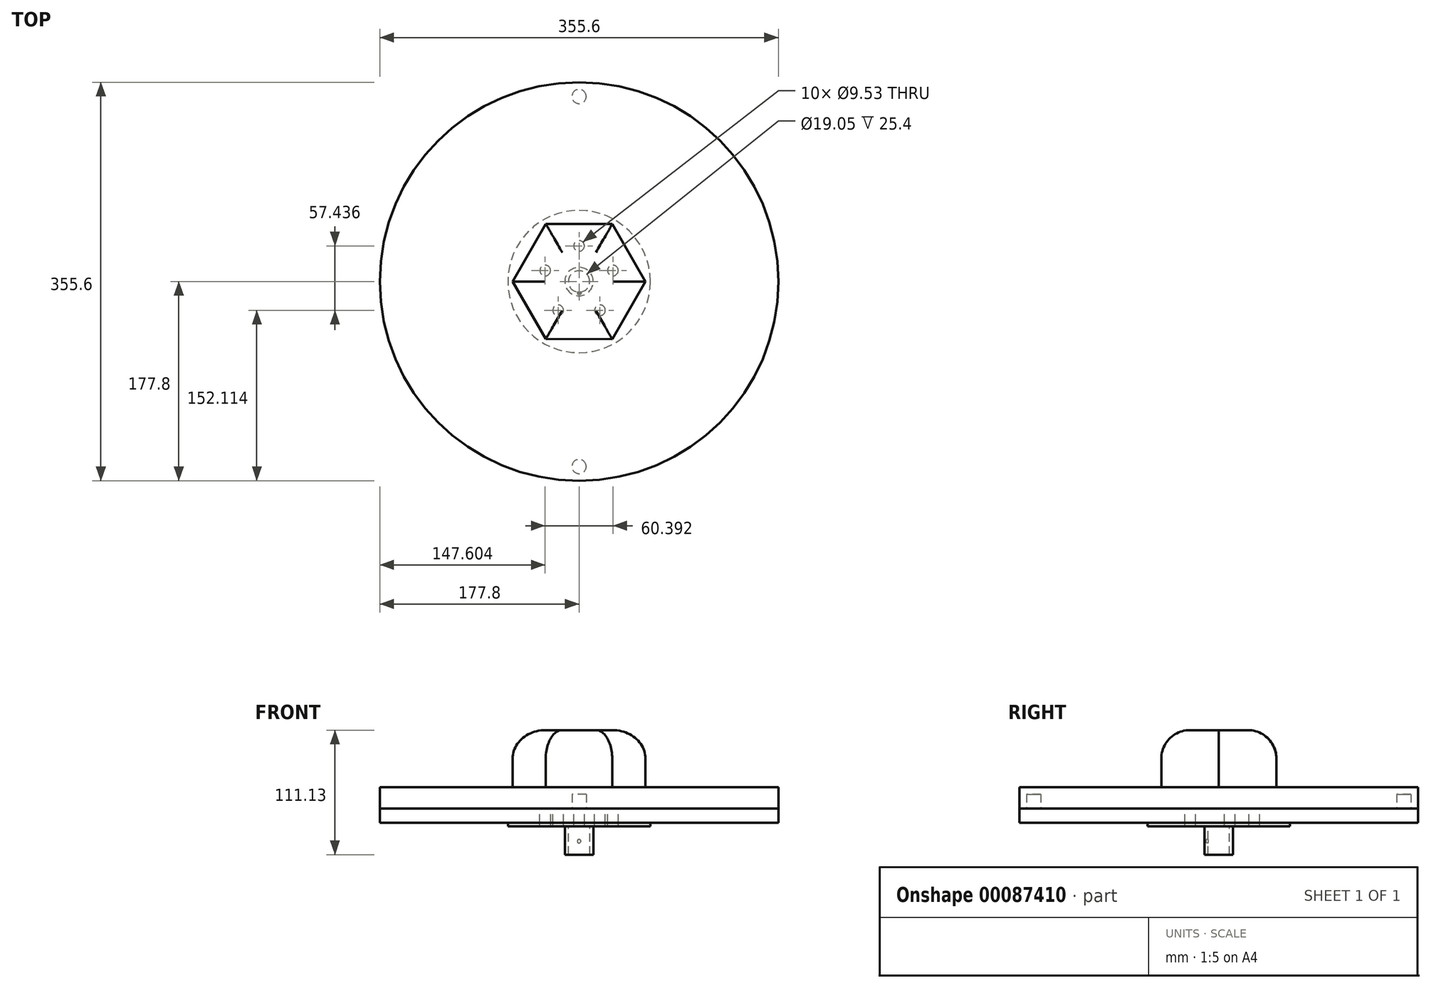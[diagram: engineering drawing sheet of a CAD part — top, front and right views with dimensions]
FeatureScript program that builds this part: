
annotation { "Feature Type Name" : "Feature", "Feature Type Description" : "" }
export const myFeature = defineFeature(function(context is Context, id is Id, definition is map)
    precondition{}
    {
        {
            var Q0;
            Q0=qCreatedBy(makeId("Top.planeOp"),FACE);
            var sketch = newSketch(context, id + "F0", { "sketchPlane" : qUnion([Q0])});
            skCircle(sketch, "E0", {"center": v(0, 0) * mm, "radius": 177.8 * mm});
            skSolve(sketch);
        }
        {
            var Q0;
            Q0 = qSketchRegion(id + "F0", true);
            var Q1;
            Q1=sQuery(id+"F0.wireOp",EDGE,"E0");
            extrude(context, id + "F1", {"entities" : qUnion([Q0]), "surfaceEntities" : qUnion([Q1]), "depth" : 12.7 * mm});
        }
        {
            var Q0;
            Q0=makeQuery(id+"F1.opExtrude","CAP_FACE",FACE,{"disambiguationData":[OSD([sQuery(id+"F0.wireOp",EDGE,"E0")])],"isStart":false});
            var sketch = newSketch(context, id + "F2", { "sketchPlane" : qUnion([Q0])});
            skCircle(sketch, "E1", {"center": v(0, 31.75) * mm, "radius": 4.76 * mm});
            skCircle(sketch, "E2.1.0", {"center": v(-30.2, 9.81) * mm, "radius": 4.76 * mm});
            skCircle(sketch, "E2.2.0", {"center": v(-18.66, -25.69) * mm, "radius": 4.76 * mm});
            skCircle(sketch, "E2.3.0", {"center": v(18.66, -25.69) * mm, "radius": 4.76 * mm});
            skCircle(sketch, "E2.4.0", {"center": v(30.2, 9.81) * mm, "radius": 4.76 * mm});
            skPoint(sketch, "E2.center", {"position": v(0, 0) * mm});
            skSolve(sketch);
        }
        {
            var Q0;
            Q0=makeQuery(id+"F1.opExtrude","CAP_FACE",FACE,{"disambiguationData":[OSD([sQuery(id+"F0.wireOp",EDGE,"E0")])],"isStart":false});
            var sketch = newSketch(context, id + "F3", { "sketchPlane" : qUnion([Q0])});
            skCircle(sketch, "E3", {"center": v(0, 165.1) * mm, "radius": 6.35 * mm});
            skCircle(sketch, "E4.1.0", {"center": v(0, -165.1) * mm, "radius": 6.35 * mm});
            skPoint(sketch, "E4.center", {"position": v(0, 0) * mm});
            skSolve(sketch);
        }
        {
            var Q0;
            Q0 = qSketchRegion(id + "F3", true);
            extrude(context, id + "F4", {"entities" : qUnion([Q0]), "operationType" : NewBodyOperationType.ADD, "depth" : 12.7 * mm});
        }
        {
            var Q0;
            Q0=makeQuery(id+"F1.opExtrude","CAP_FACE",FACE,{"disambiguationData":[OSD([sQuery(id+"F0.wireOp",EDGE,"E0")])],"isStart":false});
            var sketch = newSketch(context, id + "F5", { "sketchPlane" : qUnion([Q0])});
            skCircle(sketch, "E5.0", {"center": v(0, 0) * mm, "radius": 177.8 * mm});
            skSolve(sketch);
        }
        {
            var Q0;
            Q0 = qSketchRegion(id + "F5", true);
            extrude(context, id + "F6", {"entities" : qUnion([Q0]), "depth" : 19.05 * mm});
        }
        {
            var Q0;
            Q0=makeQuery(id+"F1.opExtrude","CAP_FACE",FACE,{"disambiguationData":[OSD([sQuery(id+"F0.wireOp",EDGE,"E0")])],"isStart":true});
            var sketch = newSketch(context, id + "F7", { "sketchPlane" : qUnion([Q0])});
            skCircle(sketch, "E6", {"center": v(0, 0) * mm, "radius": 63.5 * mm});
            skSolve(sketch);
        }
        {
            var Q0;
            Q0 = qSketchRegion(id + "F7", true);
            extrude(context, id + "F8", {"entities" : qUnion([Q0]), "depth" : 3.17 * mm});
        }
        {
            var Q0;
            Q0 = qSketchRegion(id + "F2", true);
            extrude(context, id + "F9", {"entities" : qUnion([Q0]), "operationType" : NewBodyOperationType.REMOVE, "endBound" : BoundingType.THROUGH_ALL, "oppositeDirection" : true, "depth" : 25.4 * mm});
        }
        {
            var Q0;
            Q0=makeQuery(id+"F8.opExtrude","CAP_FACE",FACE,{"disambiguationData":[OSD([sQuery(id+"F7.wireOp",EDGE,"E6")])],"isStart":false});
            var sketch = newSketch(context, id + "F10", { "sketchPlane" : qUnion([Q0])});
            skCircle(sketch, "E7", {"center": v(0, 0) * mm, "radius": 9.53 * mm});
            skCircle(sketch, "E8.0", {"center": v(0, 0) * mm, "radius": 12.7 * mm});
            skSolve(sketch);
        }
        {
            var Q0;
            Q0 = qSketchRegion(id + "F10", true);
            extrude(context, id + "F11", {"entities" : qUnion([Q0]), "operationType" : NewBodyOperationType.ADD, "depth" : 25.4 * mm});
        }
        {
            var Q0;
            Q0=qCreatedBy(makeId("Front.planeOp"),FACE);
            cPlane(context, id + "F12", {"entities" : qUnion([Q0]), "cplaneType" : CPlaneType.OFFSET, "offset" : 11.1 * mm, "width" : 152.4 * mm, "height" : 152.4 * mm});
        }
        {
            var Q0;
            Q0=qCreatedBy(id+"F12.planeOp",FACE);
            var sketch = newSketch(context, id + "F13", { "sketchPlane" : qUnion([Q0])});
            skCircle(sketch, "E9", {"center": v(0, -16.6) * mm, "radius": 1.59 * mm});
            skSolve(sketch);
        }
        {
            var Q0;
            Q0 = qSketchRegion(id + "F13", true);
            extrude(context, id + "F14", {"entities" : qUnion([Q0]), "operationType" : NewBodyOperationType.REMOVE, "endBound" : BoundingType.UP_TO_NEXT, "oppositeDirection" : true, "depth" : 25.4 * mm});
        }
        {
            var Q0;
            Q0=makeQuery(id+"F6.opExtrude","CAP_FACE",FACE,{"disambiguationData":[OSD([sQuery(id+"F5.wireOp",EDGE,"E5.0")])],"isStart":false});
            var sketch = newSketch(context, id + "F15", { "sketchPlane" : qUnion([Q0])});
            skCircle(sketch, "E10.cCircle", {"center": v(0, 0) * mm, "radius": 51.35 * mm, "construction": true});
            skLineSegment(sketch, "E10.0", {"start": v(59.29, -0.07) * mm, "end": v(29.58, -51.38) * mm});
            skLineSegment(sketch, "E10.1", {"start": v(29.58, -51.38) * mm, "end": v(-29.7, -51.3) * mm});
            skLineSegment(sketch, "E10.2", {"start": v(-29.7, -51.3) * mm, "end": v(-59.29, 0.07) * mm});
            skLineSegment(sketch, "E10.3", {"start": v(-59.29, 0.07) * mm, "end": v(-29.58, 51.38) * mm});
            skLineSegment(sketch, "E10.4", {"start": v(-29.58, 51.38) * mm, "end": v(29.7, 51.3) * mm});
            skLineSegment(sketch, "E10.5", {"start": v(29.7, 51.3) * mm, "end": v(59.29, -0.07) * mm});
            skPoint(sketch, "E10.0.midPoint", {"position": v(44.43, -25.73) * mm});
            skSolve(sketch);
        }
        {
            var Q0;
            Q0 = qSketchRegion(id + "F15", true);
            extrude(context, id + "F16", {"entities" : qUnion([Q0]), "depth" : 50.8 * mm});
        }
        {
            var Q0;
            Q0=makeQuery(id+"F16.opExtrude","CAP_EDGE",EDGE,{"disambiguationData":[OSD([sQuery(id+"F15.wireOp",EDGE,"E10.2")])],"isStart":false});
            var Q1;
            Q1=makeQuery(id+"F16.opExtrude","CAP_EDGE",EDGE,{"disambiguationData":[OSD([sQuery(id+"F15.wireOp",EDGE,"E10.4")])],"isStart":false});
            var Q2;
            Q2=makeQuery(id+"F16.opExtrude","CAP_EDGE",EDGE,{"disambiguationData":[OSD([sQuery(id+"F15.wireOp",EDGE,"E10.3")])],"isStart":false});
            var Q3;
            Q3=makeQuery(id+"F16.opExtrude","CAP_EDGE",EDGE,{"disambiguationData":[OSD([sQuery(id+"F15.wireOp",EDGE,"E10.5")])],"isStart":false});
            var Q4;
            Q4=makeQuery(id+"F16.opExtrude","CAP_EDGE",EDGE,{"disambiguationData":[OSD([sQuery(id+"F15.wireOp",EDGE,"E10.0")])],"isStart":false});
            var Q5;
            Q5=makeQuery(id+"F16.opExtrude","CAP_EDGE",EDGE,{"disambiguationData":[OSD([sQuery(id+"F15.wireOp",EDGE,"E10.1")])],"isStart":false});
            fillet(context, id + "F17", {"entities" : qUnion([Q0, Q1, Q2, Q3, Q4, Q5]), "radius" : 25.4 * mm, "tangentPropagation" : true, "allowEdgeOverflow" : false});
        }
    });
